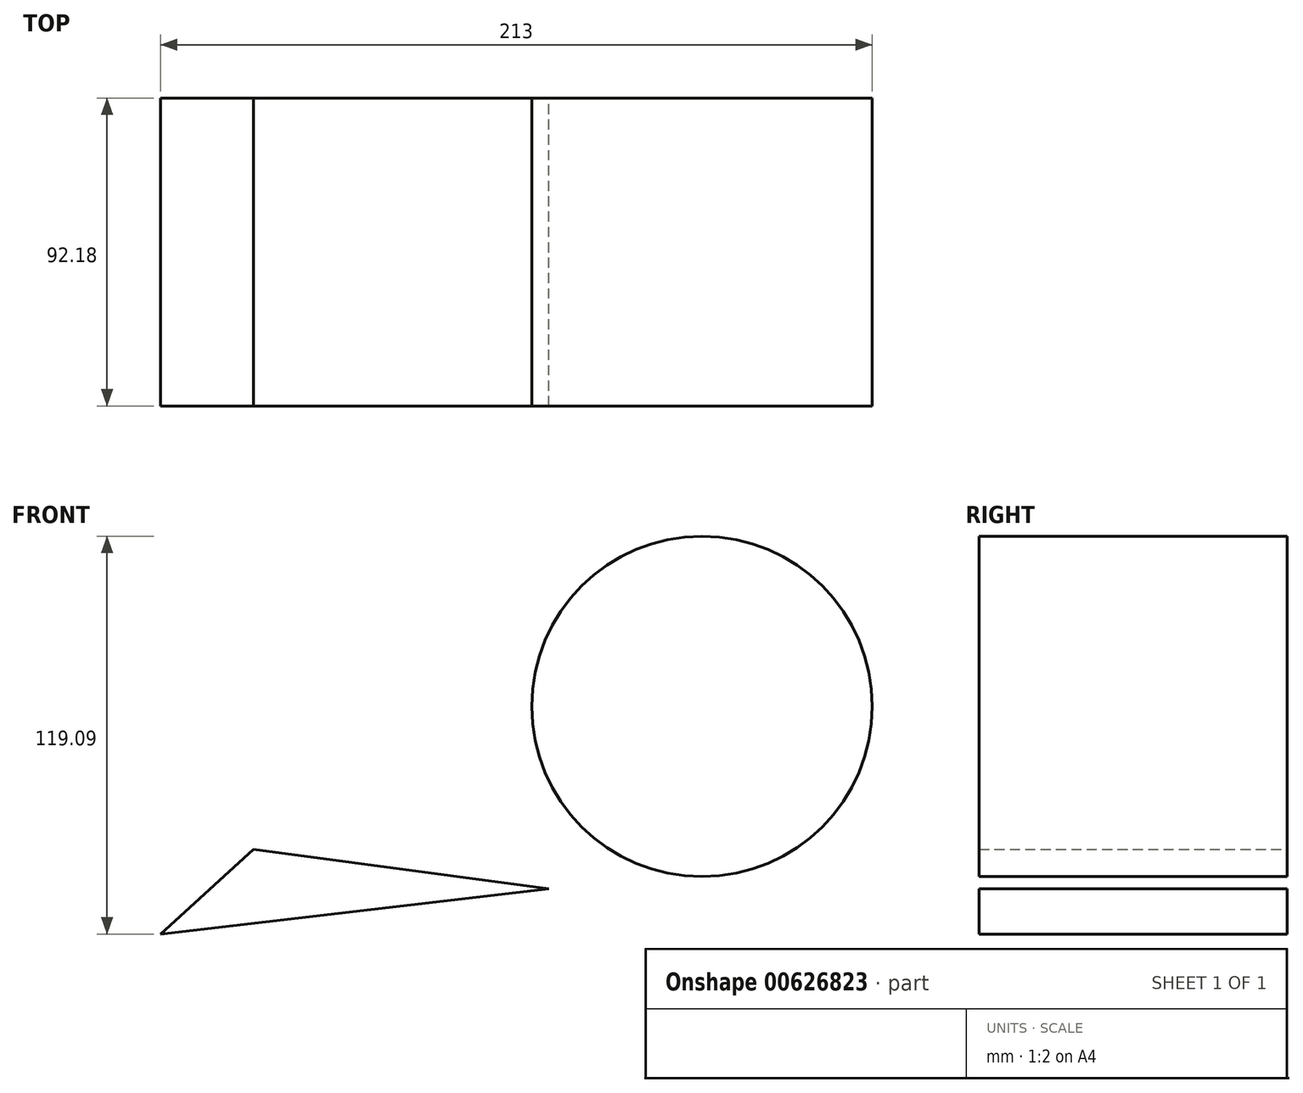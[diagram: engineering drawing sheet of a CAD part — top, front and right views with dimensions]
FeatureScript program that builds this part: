
annotation { "Feature Type Name" : "Feature", "Feature Type Description" : "" }
export const myFeature = defineFeature(function(context is Context, id is Id, definition is map)
    precondition{}
    {
        {
            var Q0;
            Q0=qCreatedBy(makeId("Front.planeOp"),FACE);
            var sketch = newSketch(context, id + "F0", { "sketchPlane" : qUnion([Q0])});
            skLineSegment(sketch, "E0", {"start": v(0, -31.7) * mm, "end": v(-27.79, -57.08) * mm});
            skLineSegment(sketch, "E1", {"start": v(-27.79, -57.08) * mm, "end": v(88.4, -43.5) * mm});
            skLineSegment(sketch, "E2", {"start": v(88.4, -43.5) * mm, "end": v(0, -31.7) * mm});
            skLineSegment(sketch, "E3", {"start": v(-176.52, -78) * mm, "end": v(-266.36, -12.98) * mm});
            skCircle(sketch, "E4", {"center": v(134.26, 11.06) * mm, "radius": 50.95 * mm});
            skSolve(sketch);
        }
        {
            var Q0;
            Q0 = qSketchRegion(id + "F0", true);
            extrude(context, id + "F1", {"entities" : qUnion([Q0]), "depth" : 92.18 * mm, "offsetDistance" : 25.4 * mm});
        }
    });
